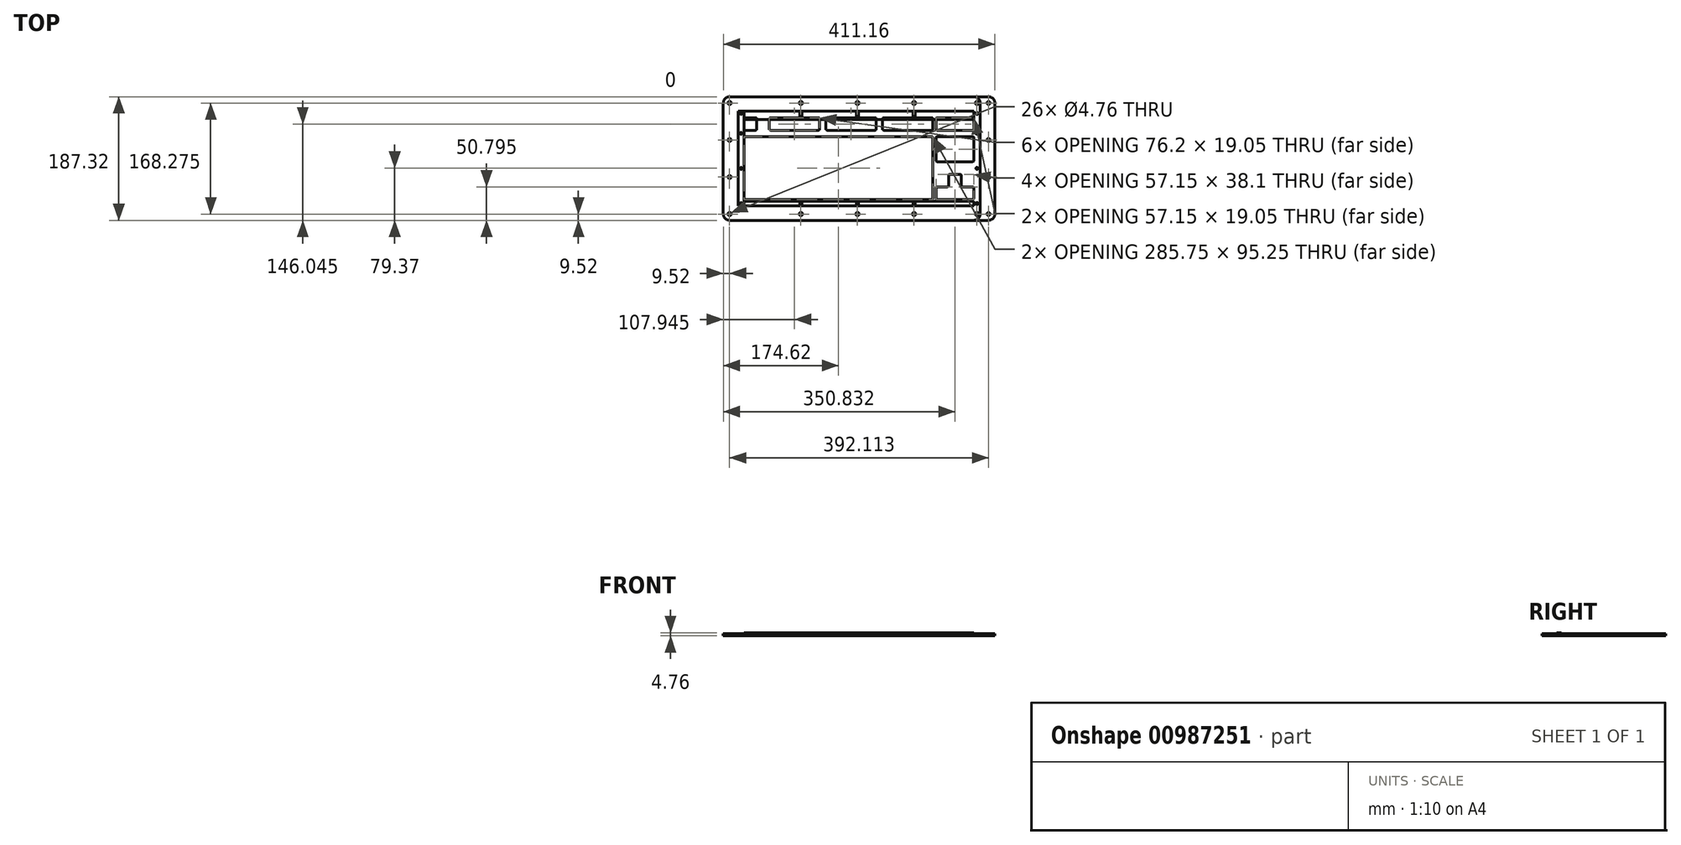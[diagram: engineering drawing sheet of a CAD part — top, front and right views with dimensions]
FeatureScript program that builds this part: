
annotation { "Feature Type Name" : "Feature", "Feature Type Description" : "" }
export const myFeature = defineFeature(function(context is Context, id is Id, definition is map)
    precondition{}
    {
        {
            var Q0;
            Q0=qCreatedBy(makeId("Top.planeOp"),FACE);
            var sketch = newSketch(context, id + "F0", { "sketchPlane" : qUnion([Q0])});
            skCircle(sketch, "E0", {"center": v(0, 104.78) * mm, "radius": 9.53 * mm, "construction": true});
            skLineSegment(sketch, "E1.bottom", {"start": v(-7.94, 114.3) * mm, "end": v(7.94, 114.3) * mm});
            skLineSegment(sketch, "E1.top", {"start": v(-7.94, 95.25) * mm, "end": v(7.94, 95.25) * mm});
            skLineSegment(sketch, "E1.left", {"start": v(-9.53, 112.71) * mm, "end": v(-9.53, 96.84) * mm});
            skLineSegment(sketch, "E1.right", {"start": v(9.53, 112.71) * mm, "end": v(9.53, 96.84) * mm});
            skCircle(sketch, "E2", {"center": v(38.1, 104.78) * mm, "radius": 9.53 * mm, "construction": true});
            skLineSegment(sketch, "E3.bottom", {"start": v(30.16, 114.3) * mm, "end": v(103.19, 114.3) * mm});
            skLineSegment(sketch, "E3.top", {"start": v(30.16, 95.25) * mm, "end": v(103.19, 95.25) * mm});
            skLineSegment(sketch, "E3.left", {"start": v(28.57, 112.71) * mm, "end": v(28.57, 96.84) * mm});
            skLineSegment(sketch, "E3.right", {"start": v(104.78, 112.71) * mm, "end": v(104.78, 96.84) * mm});
            skCircle(sketch, "E4", {"center": v(95.25, 104.78) * mm, "radius": 9.53 * mm, "construction": true});
            skCircle(sketch, "E5", {"center": v(123.83, 104.78) * mm, "radius": 9.53 * mm, "construction": true});
            skLineSegment(sketch, "E6.bottom", {"start": v(115.89, 114.3) * mm, "end": v(188.91, 114.3) * mm});
            skLineSegment(sketch, "E6.top", {"start": v(115.89, 95.25) * mm, "end": v(188.91, 95.25) * mm});
            skLineSegment(sketch, "E6.left", {"start": v(114.3, 112.71) * mm, "end": v(114.3, 96.84) * mm});
            skLineSegment(sketch, "E6.right", {"start": v(190.5, 112.71) * mm, "end": v(190.5, 96.84) * mm});
            skCircle(sketch, "E7", {"center": v(180.97, 104.78) * mm, "radius": 9.53 * mm, "construction": true});
            skCircle(sketch, "E8", {"center": v(209.55, 104.78) * mm, "radius": 9.53 * mm, "construction": true});
            skLineSegment(sketch, "E9.bottom", {"start": v(201.61, 114.3) * mm, "end": v(274.64, 114.3) * mm});
            skLineSegment(sketch, "E9.top", {"start": v(201.61, 95.25) * mm, "end": v(274.64, 95.25) * mm});
            skLineSegment(sketch, "E9.left", {"start": v(200.03, 112.71) * mm, "end": v(200.03, 96.84) * mm});
            skLineSegment(sketch, "E9.right", {"start": v(276.23, 112.71) * mm, "end": v(276.23, 96.84) * mm});
            skCircle(sketch, "E10", {"center": v(266.7, 104.78) * mm, "radius": 9.53 * mm, "construction": true});
            skCircle(sketch, "E11", {"center": v(290.51, 104.78) * mm, "radius": 9.53 * mm, "construction": true});
            skLineSegment(sketch, "E12.bottom", {"start": v(282.57, 114.3) * mm, "end": v(336.55, 114.3) * mm});
            skLineSegment(sketch, "E12.top", {"start": v(282.57, 95.25) * mm, "end": v(336.55, 95.25) * mm});
            skLineSegment(sketch, "E12.left", {"start": v(280.99, 112.71) * mm, "end": v(280.99, 96.84) * mm});
            skLineSegment(sketch, "E12.right", {"start": v(338.14, 112.71) * mm, "end": v(338.14, 96.84) * mm});
            skCircle(sketch, "E13", {"center": v(328.61, 104.78) * mm, "radius": 9.53 * mm, "construction": true});
            skLineSegment(sketch, "E14.bottom", {"start": v(-7.94, 85.73) * mm, "end": v(274.64, 85.73) * mm});
            skLineSegment(sketch, "E14.top", {"start": v(-7.94, -9.52) * mm, "end": v(274.64, -9.52) * mm});
            skLineSegment(sketch, "E14.left", {"start": v(-9.53, 84.14) * mm, "end": v(-9.53, -7.94) * mm});
            skLineSegment(sketch, "E14.right", {"start": v(276.23, 84.14) * mm, "end": v(276.23, -7.94) * mm});
            skCircle(sketch, "E15", {"center": v(0, 76.2) * mm, "radius": 9.53 * mm, "construction": true});
            skCircle(sketch, "E16", {"center": v(0, 0) * mm, "radius": 9.53 * mm, "construction": true});
            skCircle(sketch, "E17", {"center": v(290.51, 76.2) * mm, "radius": 9.53 * mm, "construction": true});
            skCircle(sketch, "E18", {"center": v(290.51, 57.15) * mm, "radius": 9.53 * mm, "construction": true});
            skCircle(sketch, "E19", {"center": v(309.56, 19.05) * mm, "radius": 9.53 * mm, "construction": true});
            skLineSegment(sketch, "E20.bottom", {"start": v(282.57, 85.72) * mm, "end": v(336.55, 85.72) * mm});
            skLineSegment(sketch, "E20.top", {"start": v(282.57, 47.63) * mm, "end": v(336.55, 47.63) * mm});
            skLineSegment(sketch, "E20.left", {"start": v(280.99, 84.14) * mm, "end": v(280.99, 49.21) * mm});
            skLineSegment(sketch, "E20.right", {"start": v(338.14, 84.14) * mm, "end": v(338.14, 49.21) * mm});
            skLineSegment(sketch, "E21", {"start": v(317.5, 28.58) * mm, "end": v(301.63, 28.58) * mm});
            skLineSegment(sketch, "E22", {"start": v(300.04, 26.99) * mm, "end": v(300.04, 11.11) * mm});
            skLineSegment(sketch, "E23", {"start": v(298.45, 9.53) * mm, "end": v(282.57, 9.53) * mm});
            skLineSegment(sketch, "E24", {"start": v(280.99, 7.94) * mm, "end": v(280.99, -7.94) * mm});
            skLineSegment(sketch, "E25", {"start": v(282.57, -9.52) * mm, "end": v(336.55, -9.52) * mm});
            skLineSegment(sketch, "E26", {"start": v(338.14, -7.94) * mm, "end": v(338.14, 7.94) * mm});
            skLineSegment(sketch, "E27", {"start": v(336.55, 9.53) * mm, "end": v(320.68, 9.53) * mm});
            skLineSegment(sketch, "E28", {"start": v(319.09, 11.11) * mm, "end": v(319.09, 26.99) * mm});
            skLineSegment(sketch, "E29", {"start": v(-9.53, -9.52) * mm, "end": v(-9.53, -41.27) * mm, "construction": true});
            skLineSegment(sketch, "E30", {"start": v(-9.53, 114.3) * mm, "end": v(-9.52, 146.05) * mm, "construction": true});
            skCircle(sketch, "E31", {"center": v(-14.29, 120.65) * mm, "radius": 1.59 * mm});
            skCircle(sketch, "E32", {"center": v(-14.29, 90.49) * mm, "radius": 1.59 * mm});
            skCircle(sketch, "E33", {"center": v(-14.29, -15.88) * mm, "radius": 1.59 * mm});
            skLineSegment(sketch, "E34", {"start": v(0, 104.78) * mm, "end": v(0, 76.2) * mm, "construction": true});
            skLineSegment(sketch, "E35", {"start": v(0, 90.49) * mm, "end": v(-14.29, 90.49) * mm, "construction": true});
            skLineSegment(sketch, "E36", {"start": v(-14.29, -15.88) * mm, "end": v(-14.29, 90.49) * mm, "construction": true});
            skCircle(sketch, "E37", {"center": v(-14.29, 37.3) * mm, "radius": 1.59 * mm});
            skCircle(sketch, "E38", {"center": v(342.9, 90.49) * mm, "radius": 1.59 * mm});
            skCircle(sketch, "E39", {"center": v(342.9, 37.3) * mm, "radius": 1.59 * mm});
            skCircle(sketch, "E40", {"center": v(342.9, -15.88) * mm, "radius": 1.59 * mm});
            skCircle(sketch, "E41", {"center": v(342.9, 120.65) * mm, "radius": 1.59 * mm});
            skCircle(sketch, "E42", {"center": v(76.2, 120.65) * mm, "radius": 1.59 * mm});
            skCircle(sketch, "E43", {"center": v(161.92, 120.65) * mm, "radius": 1.59 * mm});
            skCircle(sketch, "E44", {"center": v(247.65, 120.65) * mm, "radius": 1.59 * mm});
            skLineSegment(sketch, "E45", {"start": v(161.92, 120.65) * mm, "end": v(76.2, 120.65) * mm, "construction": true});
            skLineSegment(sketch, "E46", {"start": v(161.92, 120.65) * mm, "end": v(247.65, 120.65) * mm, "construction": true});
            skCircle(sketch, "E47", {"center": v(76.2, -15.88) * mm, "radius": 1.59 * mm});
            skCircle(sketch, "E48", {"center": v(161.92, -15.88) * mm, "radius": 1.59 * mm});
            skCircle(sketch, "E49", {"center": v(247.65, -15.88) * mm, "radius": 1.59 * mm});
            skPoint(sketch, "E50.visualSharp", {"position": v(-9.52, 114.3) * mm});
            skArc(sketch, "E50.filletArc", {"start": v(-7.94, 114.3) * mm, "mid": v(-9.06, 113.84) * mm, "end": v(-9.53, 112.71) * mm});
            skPoint(sketch, "E51.visualSharp", {"position": v(-9.53, 95.25) * mm});
            skArc(sketch, "E51.filletArc", {"start": v(-9.53, 96.84) * mm, "mid": v(-9.06, 95.71) * mm, "end": v(-7.94, 95.25) * mm});
            skPoint(sketch, "E52.visualSharp", {"position": v(9.53, 95.25) * mm});
            skArc(sketch, "E52.filletArc", {"start": v(7.94, 95.25) * mm, "mid": v(9.06, 95.71) * mm, "end": v(9.53, 96.84) * mm});
            skPoint(sketch, "E53.visualSharp", {"position": v(9.53, 114.3) * mm});
            skArc(sketch, "E53.filletArc", {"start": v(9.53, 112.71) * mm, "mid": v(9.06, 113.84) * mm, "end": v(7.94, 114.3) * mm});
            skPoint(sketch, "E54.visualSharp", {"position": v(28.57, 114.3) * mm});
            skArc(sketch, "E54.filletArc", {"start": v(30.16, 114.3) * mm, "mid": v(29.04, 113.84) * mm, "end": v(28.57, 112.71) * mm});
            skPoint(sketch, "E55.visualSharp", {"position": v(28.57, 95.25) * mm});
            skArc(sketch, "E55.filletArc", {"start": v(28.57, 96.84) * mm, "mid": v(29.04, 95.71) * mm, "end": v(30.16, 95.25) * mm});
            skPoint(sketch, "E56.visualSharp", {"position": v(104.78, 114.3) * mm});
            skArc(sketch, "E56.filletArc", {"start": v(104.78, 112.71) * mm, "mid": v(104.31, 113.84) * mm, "end": v(103.19, 114.3) * mm});
            skPoint(sketch, "E57.visualSharp", {"position": v(104.78, 95.25) * mm});
            skArc(sketch, "E57.filletArc", {"start": v(103.19, 95.25) * mm, "mid": v(104.31, 95.71) * mm, "end": v(104.78, 96.84) * mm});
            skPoint(sketch, "E58.visualSharp", {"position": v(114.3, 95.25) * mm});
            skArc(sketch, "E58.filletArc", {"start": v(114.3, 96.84) * mm, "mid": v(114.76, 95.71) * mm, "end": v(115.89, 95.25) * mm});
            skPoint(sketch, "E59.visualSharp", {"position": v(114.3, 114.3) * mm});
            skArc(sketch, "E59.filletArc", {"start": v(115.89, 114.3) * mm, "mid": v(114.76, 113.84) * mm, "end": v(114.3, 112.71) * mm});
            skPoint(sketch, "E60.visualSharp", {"position": v(190.5, 114.3) * mm});
            skArc(sketch, "E60.filletArc", {"start": v(190.5, 112.71) * mm, "mid": v(190.04, 113.84) * mm, "end": v(188.91, 114.3) * mm});
            skPoint(sketch, "E61.visualSharp", {"position": v(190.5, 95.25) * mm});
            skArc(sketch, "E61.filletArc", {"start": v(188.91, 95.25) * mm, "mid": v(190.04, 95.71) * mm, "end": v(190.5, 96.84) * mm});
            skPoint(sketch, "E62.visualSharp", {"position": v(200.03, 95.25) * mm});
            skArc(sketch, "E62.filletArc", {"start": v(200.03, 96.84) * mm, "mid": v(200.49, 95.71) * mm, "end": v(201.61, 95.25) * mm});
            skPoint(sketch, "E63.visualSharp", {"position": v(200.03, 114.3) * mm});
            skArc(sketch, "E63.filletArc", {"start": v(201.61, 114.3) * mm, "mid": v(200.49, 113.84) * mm, "end": v(200.03, 112.71) * mm});
            skPoint(sketch, "E64.visualSharp", {"position": v(276.23, 114.3) * mm});
            skArc(sketch, "E64.filletArc", {"start": v(276.23, 112.71) * mm, "mid": v(275.76, 113.84) * mm, "end": v(274.64, 114.3) * mm});
            skPoint(sketch, "E65.visualSharp", {"position": v(276.23, 95.25) * mm});
            skArc(sketch, "E65.filletArc", {"start": v(274.64, 95.25) * mm, "mid": v(275.76, 95.71) * mm, "end": v(276.23, 96.84) * mm});
            skPoint(sketch, "E66.visualSharp", {"position": v(280.99, 114.3) * mm});
            skArc(sketch, "E66.filletArc", {"start": v(282.57, 114.3) * mm, "mid": v(281.45, 113.84) * mm, "end": v(280.99, 112.71) * mm});
            skPoint(sketch, "E67.visualSharp", {"position": v(338.14, 114.3) * mm});
            skArc(sketch, "E67.filletArc", {"start": v(338.14, 112.71) * mm, "mid": v(337.67, 113.84) * mm, "end": v(336.55, 114.3) * mm});
            skPoint(sketch, "E68.visualSharp", {"position": v(338.14, 95.25) * mm});
            skArc(sketch, "E68.filletArc", {"start": v(336.55, 95.25) * mm, "mid": v(337.67, 95.71) * mm, "end": v(338.14, 96.84) * mm});
            skPoint(sketch, "E69.visualSharp", {"position": v(280.99, 95.25) * mm});
            skArc(sketch, "E69.filletArc", {"start": v(280.99, 96.84) * mm, "mid": v(281.45, 95.71) * mm, "end": v(282.57, 95.25) * mm});
            skPoint(sketch, "E70.visualSharp", {"position": v(-9.53, 85.73) * mm});
            skArc(sketch, "E70.filletArc", {"start": v(-7.94, 85.73) * mm, "mid": v(-9.06, 85.26) * mm, "end": v(-9.53, 84.14) * mm});
            skPoint(sketch, "E71.visualSharp", {"position": v(-9.53, -9.52) * mm});
            skArc(sketch, "E71.filletArc", {"start": v(-9.53, -7.94) * mm, "mid": v(-9.06, -9.06) * mm, "end": v(-7.94, -9.52) * mm});
            skPoint(sketch, "E72.visualSharp", {"position": v(276.23, 85.73) * mm});
            skArc(sketch, "E72.filletArc", {"start": v(276.23, 84.14) * mm, "mid": v(275.76, 85.26) * mm, "end": v(274.64, 85.73) * mm});
            skPoint(sketch, "E73.visualSharp", {"position": v(276.23, -9.52) * mm});
            skArc(sketch, "E73.filletArc", {"start": v(274.64, -9.52) * mm, "mid": v(275.76, -9.06) * mm, "end": v(276.23, -7.94) * mm});
            skPoint(sketch, "E74.visualSharp", {"position": v(280.99, 9.53) * mm});
            skArc(sketch, "E74.filletArc", {"start": v(282.57, 9.53) * mm, "mid": v(281.45, 9.06) * mm, "end": v(280.99, 7.94) * mm});
            skPoint(sketch, "E75.visualSharp", {"position": v(280.99, -9.52) * mm});
            skArc(sketch, "E75.filletArc", {"start": v(280.99, -7.94) * mm, "mid": v(281.45, -9.06) * mm, "end": v(282.57, -9.52) * mm});
            skPoint(sketch, "E76.visualSharp", {"position": v(338.14, -9.52) * mm});
            skArc(sketch, "E76.filletArc", {"start": v(336.55, -9.52) * mm, "mid": v(337.67, -9.06) * mm, "end": v(338.14, -7.94) * mm});
            skPoint(sketch, "E77.visualSharp", {"position": v(338.14, 9.53) * mm});
            skArc(sketch, "E77.filletArc", {"start": v(338.14, 7.94) * mm, "mid": v(337.67, 9.06) * mm, "end": v(336.55, 9.53) * mm});
            skPoint(sketch, "E78.visualSharp", {"position": v(319.09, 28.58) * mm});
            skArc(sketch, "E78.filletArc", {"start": v(319.09, 26.99) * mm, "mid": v(318.62, 28.11) * mm, "end": v(317.5, 28.58) * mm});
            skPoint(sketch, "E79.visualSharp", {"position": v(300.04, 28.58) * mm});
            skArc(sketch, "E79.filletArc", {"start": v(301.63, 28.58) * mm, "mid": v(300.5, 28.11) * mm, "end": v(300.04, 26.99) * mm});
            skPoint(sketch, "E80.visualSharp", {"position": v(300.04, 9.53) * mm});
            skArc(sketch, "E80.filletArc", {"start": v(298.45, 9.53) * mm, "mid": v(299.57, 9.99) * mm, "end": v(300.04, 11.11) * mm});
            skPoint(sketch, "E81.visualSharp", {"position": v(319.09, 9.53) * mm});
            skArc(sketch, "E81.filletArc", {"start": v(319.09, 11.11) * mm, "mid": v(319.55, 9.99) * mm, "end": v(320.68, 9.53) * mm});
            skPoint(sketch, "E82.visualSharp", {"position": v(280.99, 85.72) * mm});
            skArc(sketch, "E82.filletArc", {"start": v(282.57, 85.72) * mm, "mid": v(281.45, 85.26) * mm, "end": v(280.99, 84.14) * mm});
            skPoint(sketch, "E83.visualSharp", {"position": v(280.99, 47.63) * mm});
            skArc(sketch, "E83.filletArc", {"start": v(280.99, 49.21) * mm, "mid": v(281.45, 48.09) * mm, "end": v(282.57, 47.63) * mm});
            skPoint(sketch, "E84.visualSharp", {"position": v(338.14, 85.72) * mm});
            skArc(sketch, "E84.filletArc", {"start": v(338.14, 84.14) * mm, "mid": v(337.67, 85.26) * mm, "end": v(336.55, 85.72) * mm});
            skPoint(sketch, "E85.visualSharp", {"position": v(338.14, 47.63) * mm});
            skArc(sketch, "E85.filletArc", {"start": v(336.55, 47.63) * mm, "mid": v(337.67, 48.09) * mm, "end": v(338.14, 49.21) * mm});
            skLineSegment(sketch, "E86", {"start": v(95.25, 104.78) * mm, "end": v(38.1, 104.78) * mm, "construction": true});
            skLineSegment(sketch, "E87", {"start": v(123.83, 104.78) * mm, "end": v(180.97, 104.78) * mm, "construction": true});
            skLineSegment(sketch, "E88", {"start": v(209.55, 104.78) * mm, "end": v(266.7, 104.78) * mm, "construction": true});
            skLineSegment(sketch, "E89", {"start": v(0, 117.22) * mm, "end": v(-9.65, 117.22) * mm, "construction": true});
            skLineSegment(sketch, "E90", {"start": v(-9.65, 117.22) * mm, "end": v(-9.65, 104.78) * mm, "construction": true});
            skSolve(sketch);
        }
        {
            var Q0;
            Q0=qCreatedBy(makeId("Top.planeOp"),FACE);
            var sketch = newSketch(context, id + "F1", { "sketchPlane" : qUnion([Q0])});
            skLineSegment(sketch, "E91.bottom", {"start": v(-41.28, 146.05) * mm, "end": v(347.66, 146.05) * mm});
            skLineSegment(sketch, "E91.top", {"start": v(-41.28, -41.28) * mm, "end": v(347.66, -41.27) * mm});
            skLineSegment(sketch, "E91.right", {"start": v(347.66, 146.05) * mm, "end": v(347.66, -41.27) * mm});
            skLineSegment(sketch, "E92", {"start": v(-41.28, 146.05) * mm, "end": v(-41.28, -41.28) * mm});
            skCircle(sketch, "E93", {"center": v(-31.75, 136.53) * mm, "radius": 2.38 * mm});
            skCircle(sketch, "E94", {"center": v(-31.75, 80.43) * mm, "radius": 2.38 * mm});
            skCircle(sketch, "E95", {"center": v(-31.75, 24.34) * mm, "radius": 2.38 * mm});
            skCircle(sketch, "E96", {"center": v(-31.75, -31.75) * mm, "radius": 2.38 * mm});
            skCircle(sketch, "E97", {"center": v(76.2, 136.53) * mm, "radius": 2.38 * mm});
            skCircle(sketch, "E98", {"center": v(161.92, 136.53) * mm, "radius": 2.38 * mm});
            skCircle(sketch, "E99", {"center": v(247.65, 136.53) * mm, "radius": 2.38 * mm});
            skCircle(sketch, "E100", {"center": v(247.65, -31.75) * mm, "radius": 2.38 * mm});
            skCircle(sketch, "E101", {"center": v(161.93, -31.75) * mm, "radius": 2.38 * mm});
            skCircle(sketch, "E102", {"center": v(76.2, -31.75) * mm, "radius": 2.38 * mm});
            skCircle(sketch, "E103", {"center": v(342.9, 136.53) * mm, "radius": 2.38 * mm});
            skCircle(sketch, "E104", {"center": v(342.9, -31.75) * mm, "radius": 2.38 * mm});
            skLineSegment(sketch, "E105", {"start": v(-31.75, 136.53) * mm, "end": v(-31.75, 80.43) * mm, "construction": true});
            skLineSegment(sketch, "E106", {"start": v(-31.75, 80.43) * mm, "end": v(-31.75, 24.34) * mm, "construction": true});
            skLineSegment(sketch, "E107", {"start": v(-31.75, 24.34) * mm, "end": v(-31.75, -31.75) * mm, "construction": true});
            skLineSegment(sketch, "E108", {"start": v(-31.75, -31.75) * mm, "end": v(-31.75, -41.28) * mm, "construction": true});
            skLineSegment(sketch, "E109", {"start": v(-31.75, 136.53) * mm, "end": v(-31.75, 146.05) * mm, "construction": true});
            skLineSegment(sketch, "E110", {"start": v(-31.75, 136.53) * mm, "end": v(-41.28, 136.53) * mm, "construction": true});
            skSolve(sketch);
        }
        {
            var Q0;
            Q0 = qSketchRegion(id + "F1", true);
            extrude(context, id + "F2", {"entities" : qUnion([Q0]), "depth" : 3.17 * mm, "offsetDistance" : 25.4 * mm});
        }
        {
            var Q0;
            Q0 = qSketchRegion(id + "F0", true);
            extrude(context, id + "F3", {"entities" : qUnion([Q0]), "operationType" : NewBodyOperationType.REMOVE, "endBound" : BoundingType.THROUGH_ALL, "depth" : 25.4 * mm, "offsetDistance" : 25.4 * mm});
        }
        {
            var Q0;
            Q0=qCreatedBy(makeId("Top.planeOp"),FACE);
            var sketch = newSketch(context, id + "F4", { "sketchPlane" : qUnion([Q0])});
            skLineSegment(sketch, "E111.bottom", {"start": v(-41.28, 146.05) * mm, "end": v(369.89, 146.05) * mm});
            skLineSegment(sketch, "E111.top", {"start": v(-41.28, -41.27) * mm, "end": v(369.89, -41.27) * mm});
            skLineSegment(sketch, "E111.left", {"start": v(-41.28, 146.05) * mm, "end": v(-41.27, -41.27) * mm});
            skLineSegment(sketch, "E111.right", {"start": v(369.89, 146.05) * mm, "end": v(369.89, -41.27) * mm});
            skCircle(sketch, "E112", {"center": v(-31.75, 136.53) * mm, "radius": 2.38 * mm});
            skCircle(sketch, "E113", {"center": v(-31.75, 80.43) * mm, "radius": 2.38 * mm});
            skCircle(sketch, "E114", {"center": v(-31.75, 24.34) * mm, "radius": 2.38 * mm});
            skCircle(sketch, "E115", {"center": v(-31.75, -31.75) * mm, "radius": 2.38 * mm});
            skLineSegment(sketch, "E116", {"start": v(-31.75, 136.53) * mm, "end": v(-31.75, 80.43) * mm, "construction": true});
            skLineSegment(sketch, "E117", {"start": v(-31.75, -31.75) * mm, "end": v(-31.75, 24.34) * mm, "construction": true});
            skLineSegment(sketch, "E118", {"start": v(-31.75, 80.43) * mm, "end": v(-31.75, 24.34) * mm, "construction": true});
            skCircle(sketch, "E119", {"center": v(360.36, 136.53) * mm, "radius": 2.38 * mm});
            skCircle(sketch, "E120", {"center": v(76.2, 136.53) * mm, "radius": 2.38 * mm});
            skCircle(sketch, "E121", {"center": v(161.92, 136.53) * mm, "radius": 2.38 * mm});
            skCircle(sketch, "E122", {"center": v(247.65, 136.53) * mm, "radius": 2.38 * mm});
            skLineSegment(sketch, "E123", {"start": v(-31.75, 136.53) * mm, "end": v(76.2, 136.53) * mm, "construction": true});
            skLineSegment(sketch, "E124", {"start": v(76.2, 136.53) * mm, "end": v(161.92, 136.53) * mm, "construction": true});
            skLineSegment(sketch, "E125", {"start": v(161.92, 136.53) * mm, "end": v(247.65, 136.53) * mm, "construction": true});
            skLineSegment(sketch, "E126", {"start": v(247.65, 136.53) * mm, "end": v(360.36, 136.53) * mm, "construction": true});
            skCircle(sketch, "E127", {"center": v(360.36, 80.43) * mm, "radius": 2.38 * mm});
            skCircle(sketch, "E128", {"center": v(360.36, 24.34) * mm, "radius": 2.38 * mm});
            skCircle(sketch, "E129", {"center": v(360.36, -31.75) * mm, "radius": 2.38 * mm});
            skLineSegment(sketch, "E130", {"start": v(360.36, 136.53) * mm, "end": v(360.36, 80.43) * mm, "construction": true});
            skLineSegment(sketch, "E131", {"start": v(360.36, 80.43) * mm, "end": v(360.36, 24.34) * mm, "construction": true});
            skLineSegment(sketch, "E132", {"start": v(360.36, 24.34) * mm, "end": v(360.36, -31.75) * mm, "construction": true});
            skCircle(sketch, "E133", {"center": v(76.2, -31.75) * mm, "radius": 2.38 * mm});
            skCircle(sketch, "E134", {"center": v(161.92, -31.75) * mm, "radius": 2.38 * mm});
            skCircle(sketch, "E135", {"center": v(247.65, -31.75) * mm, "radius": 2.38 * mm});
            skLineSegment(sketch, "E136", {"start": v(76.2, -31.75) * mm, "end": v(161.92, -31.75) * mm, "construction": true});
            skLineSegment(sketch, "E137", {"start": v(161.92, -31.75) * mm, "end": v(247.65, -31.75) * mm, "construction": true});
            skLineSegment(sketch, "E138", {"start": v(-31.75, 136.53) * mm, "end": v(-31.75, 146.05) * mm, "construction": true});
            skLineSegment(sketch, "E139", {"start": v(-31.75, 136.53) * mm, "end": v(-41.28, 136.53) * mm, "construction": true});
            skLineSegment(sketch, "E140", {"start": v(-31.75, -31.75) * mm, "end": v(-31.75, -41.27) * mm, "construction": true});
            skLineSegment(sketch, "E141", {"start": v(360.36, 136.53) * mm, "end": v(369.89, 136.53) * mm, "construction": true});
            skSolve(sketch);
        }
        {
            var Q0;
            Q0 = qSketchRegion(id + "F4", true);
            extrude(context, id + "F5", {"entities" : qUnion([Q0]), "depth" : 3.17 * mm, "offsetDistance" : 25.4 * mm});
        }
        {
            var Q0;
            Q0 = qSketchRegion(id + "F0", true);
            extrude(context, id + "F6", {"entities" : qUnion([Q0]), "operationType" : NewBodyOperationType.REMOVE, "endBound" : BoundingType.UP_TO_NEXT, "depth" : 25.4 * mm, "offsetDistance" : 25.4 * mm});
        }
        {
            var Q0;
            Q0=qCreatedBy(makeId("Top.planeOp"),FACE);
            var sketch = newSketch(context, id + "F7", { "sketchPlane" : qUnion([Q0])});
            skLineSegment(sketch, "E142.bottom", {"start": v(-9.84, 124.08) * mm, "end": v(-18.73, 124.08) * mm});
            skLineSegment(sketch, "E142.top", {"start": v(-9.84, -19.3) * mm, "end": v(-18.73, -19.3) * mm});
            skLineSegment(sketch, "E142.left", {"start": v(-9.84, 124.08) * mm, "end": v(-9.84, -19.3) * mm});
            skLineSegment(sketch, "E142.right", {"start": v(-18.73, 124.08) * mm, "end": v(-18.73, -19.3) * mm});
            skCircle(sketch, "E143", {"center": v(-14.29, 120.65) * mm, "radius": 1.59 * mm});
            skCircle(sketch, "E144", {"center": v(-14.29, 90.49) * mm, "radius": 1.59 * mm});
            skCircle(sketch, "E145", {"center": v(-14.29, 37.3) * mm, "radius": 1.59 * mm});
            skCircle(sketch, "E146", {"center": v(-14.29, -15.88) * mm, "radius": 1.59 * mm});
            skLineSegment(sketch, "E147", {"start": v(-14.29, 120.65) * mm, "end": v(-9.84, 120.65) * mm, "construction": true});
            skLineSegment(sketch, "E148", {"start": v(-14.29, 120.65) * mm, "end": v(-18.73, 120.65) * mm, "construction": true});
            skLineSegment(sketch, "E149", {"start": v(-14.29, 120.65) * mm, "end": v(-14.29, 124.08) * mm, "construction": true});
            skLineSegment(sketch, "E150", {"start": v(-14.29, -15.88) * mm, "end": v(-14.29, -19.3) * mm, "construction": true});
            skSolve(sketch);
        }
        {
            var Q0;
            Q0 = qSketchRegion(id + "F7", true);
            extrude(context, id + "F8", {"entities" : qUnion([Q0]), "depth" : 3.17 * mm, "offsetDistance" : 25.4 * mm});
        }
        {
            var Q0;
            Q0=qCreatedBy(makeId("Top.planeOp"),FACE);
            var sketch = newSketch(context, id + "F9", { "sketchPlane" : qUnion([Q0])});
            skLineSegment(sketch, "E151.bottom", {"start": v(-9.84, 124.08) * mm, "end": v(338.4, 124.08) * mm});
            skLineSegment(sketch, "E151.top", {"start": v(-9.84, 111.38) * mm, "end": v(338.4, 111.38) * mm});
            skLineSegment(sketch, "E151.left", {"start": v(-9.84, 124.08) * mm, "end": v(-9.84, 111.38) * mm});
            skLineSegment(sketch, "E151.right", {"start": v(338.4, 124.08) * mm, "end": v(338.4, 111.38) * mm});
            skArc(sketch, "E152", {"start": v(77.79, 121.44) * mm, "mid": v(76.2, 123.03) * mm, "end": v(74.61, 121.44) * mm});
            skArc(sketch, "E153", {"start": v(74.61, 117.63) * mm, "mid": v(76.2, 116.05) * mm, "end": v(77.79, 117.63) * mm});
            skLineSegment(sketch, "E154", {"start": v(77.79, 121.44) * mm, "end": v(77.79, 117.63) * mm});
            skLineSegment(sketch, "E155", {"start": v(74.61, 121.44) * mm, "end": v(74.61, 117.63) * mm});
            skArc(sketch, "E156", {"start": v(163.51, 121.44) * mm, "mid": v(161.92, 123.03) * mm, "end": v(160.34, 121.44) * mm});
            skArc(sketch, "E157", {"start": v(160.34, 117.63) * mm, "mid": v(161.92, 116.05) * mm, "end": v(163.51, 117.63) * mm});
            skLineSegment(sketch, "E158", {"start": v(163.51, 121.44) * mm, "end": v(163.51, 117.63) * mm});
            skLineSegment(sketch, "E159", {"start": v(160.34, 117.63) * mm, "end": v(160.34, 121.44) * mm});
            skArc(sketch, "E160", {"start": v(249.24, 121.44) * mm, "mid": v(247.65, 123.03) * mm, "end": v(246.06, 121.44) * mm});
            skArc(sketch, "E161", {"start": v(246.06, 117.63) * mm, "mid": v(247.65, 116.05) * mm, "end": v(249.24, 117.63) * mm});
            skLineSegment(sketch, "E162", {"start": v(249.24, 121.44) * mm, "end": v(249.24, 117.63) * mm});
            skLineSegment(sketch, "E163", {"start": v(246.06, 121.44) * mm, "end": v(246.06, 117.63) * mm});
            skSolve(sketch);
        }
        {
            var Q0;
            Q0=makeQuery(id+"F9.imprint","IMPRINT",FACE,{"disambiguationData":[TD([[makeQuery(id+"F9.imprint","IMPRINT",EDGE,{"derivedFrom":sQuery(id+"F9.wireOp",EDGE,"E151.bottom")}),-1.0]])]});
            extrude(context, id + "F10", {"entities" : qUnion([Q0]), "depth" : 3.17 * mm, "offsetDistance" : 25.4 * mm});
        }
        {
            var Q0;
            Q0=qCreatedBy(makeId("Top.planeOp"),FACE);
            var sketch = newSketch(context, id + "F11", { "sketchPlane" : qUnion([Q0])});
            skLineSegment(sketch, "E164.bottom", {"start": v(-9.84, -19.3) * mm, "end": v(338.46, -19.3) * mm});
            skLineSegment(sketch, "E164.top", {"start": v(-9.84, -12.45) * mm, "end": v(338.46, -12.45) * mm});
            skLineSegment(sketch, "E164.left", {"start": v(-9.84, -19.3) * mm, "end": v(-9.84, -12.45) * mm});
            skLineSegment(sketch, "E164.right", {"start": v(338.46, -19.3) * mm, "end": v(338.46, -12.45) * mm});
            skCircle(sketch, "E165", {"center": v(247.65, -15.88) * mm, "radius": 1.59 * mm});
            skCircle(sketch, "E166", {"center": v(161.92, -15.88) * mm, "radius": 1.59 * mm});
            skCircle(sketch, "E167", {"center": v(76.2, -15.88) * mm, "radius": 1.59 * mm});
            skLineSegment(sketch, "E168", {"start": v(-9.84, -15.88) * mm, "end": v(-14.29, -15.88) * mm, "construction": true});
            skSolve(sketch);
        }
        {
            var Q0;
            Q0 = qSketchRegion(id + "F11", true);
            extrude(context, id + "F12", {"entities" : qUnion([Q0]), "depth" : 4.76 * mm, "offsetDistance" : 25.4 * mm});
        }
        {
            var Q0;
            Q0=makeQuery(id+"F5.opExtrude","SWEPT_EDGE",EDGE,{"disambiguationData":[OSD([sQuery(id+"F4.wireOp",EDGE,"E111.top"),sQuery(id+"F4.wireOp",EDGE,"E111.left")])]});
            var Q1;
            Q1=makeQuery(id+"F5.opExtrude","SWEPT_EDGE",EDGE,{"disambiguationData":[OSD([sQuery(id+"F4.wireOp",EDGE,"E111.bottom"),sQuery(id+"F4.wireOp",EDGE,"E111.left")])]});
            var Q2;
            Q2=makeQuery(id+"F5.opExtrude","SWEPT_EDGE",EDGE,{"disambiguationData":[OSD([sQuery(id+"F4.wireOp",EDGE,"E111.bottom"),sQuery(id+"F4.wireOp",EDGE,"E111.right")])]});
            var Q3;
            Q3=makeQuery(id+"F5.opExtrude","SWEPT_EDGE",EDGE,{"disambiguationData":[OSD([sQuery(id+"F4.wireOp",EDGE,"E111.top"),sQuery(id+"F4.wireOp",EDGE,"E111.right")])]});
            fillet(context, id + "F13", {"entities" : qUnion([Q0, Q1, Q2, Q3]), "radius" : 9.52 * mm, "tangentPropagation" : true, "allowEdgeOverflow" : false});
        }
        {
            var Q0;
            Q0=makeQuery(id+"F2.opExtrude","SWEPT_EDGE",EDGE,{"disambiguationData":[OSD([sQuery(id+"F1.wireOp",EDGE,"E91.top"),sQuery(id+"F1.wireOp",EDGE,"E92")])]});
            var Q1;
            Q1=makeQuery(id+"F2.opExtrude","SWEPT_EDGE",EDGE,{"disambiguationData":[OSD([sQuery(id+"F1.wireOp",EDGE,"E91.bottom"),sQuery(id+"F1.wireOp",EDGE,"E92")])]});
            var Q2;
            Q2=makeQuery(id+"F2.opExtrude","SWEPT_EDGE",EDGE,{"disambiguationData":[OSD([sQuery(id+"F1.wireOp",EDGE,"E91.bottom"),sQuery(id+"F1.wireOp",EDGE,"E91.right")])]});
            var Q3;
            Q3=makeQuery(id+"F2.opExtrude","SWEPT_EDGE",EDGE,{"disambiguationData":[OSD([sQuery(id+"F1.wireOp",EDGE,"E91.top"),sQuery(id+"F1.wireOp",EDGE,"E91.right")])]});
            fillet(context, id + "F14", {"entities" : qUnion([Q0, Q1, Q2, Q3]), "radius" : 9.52 * mm, "tangentPropagation" : true, "allowEdgeOverflow" : false});
        }
    });
